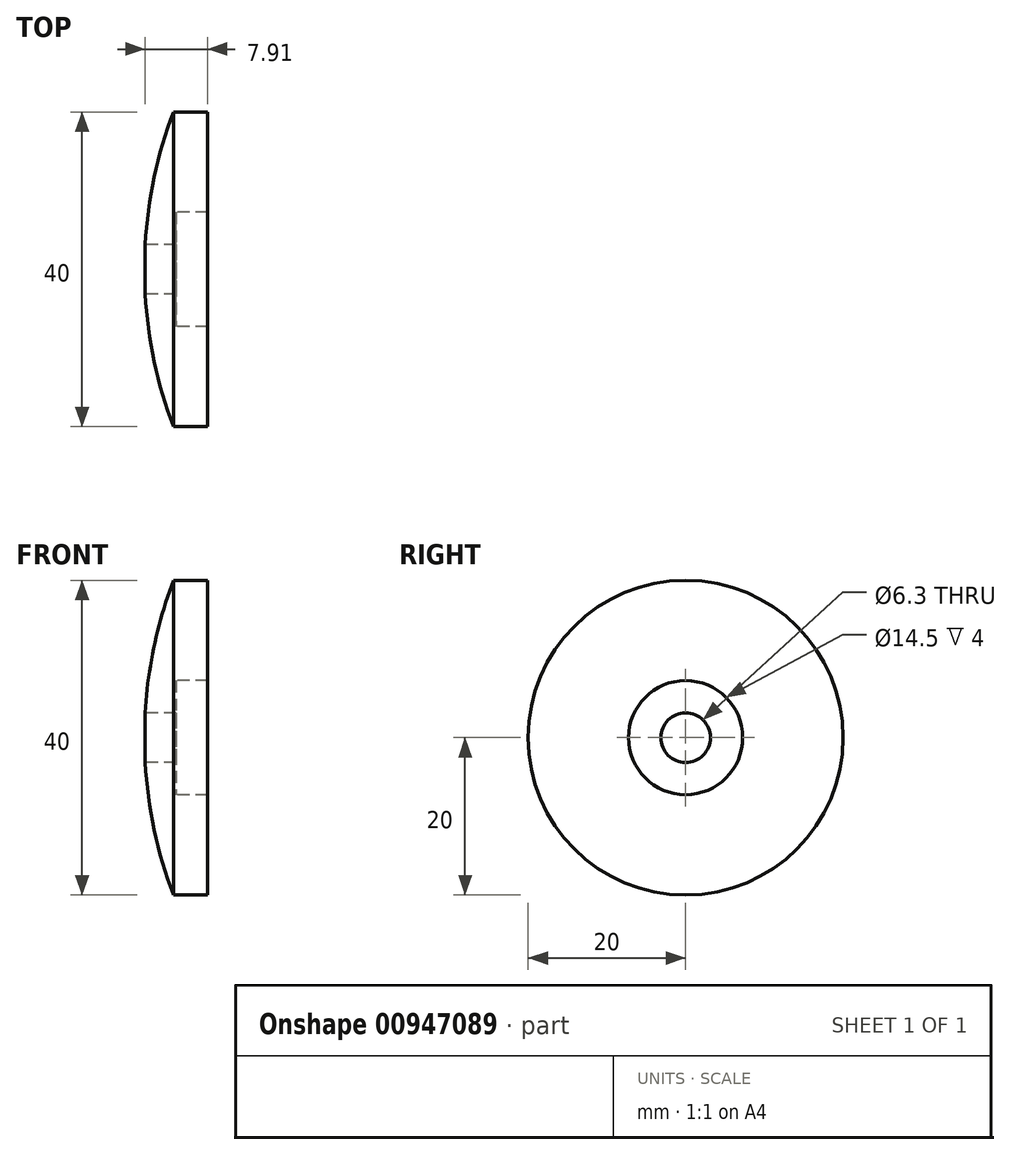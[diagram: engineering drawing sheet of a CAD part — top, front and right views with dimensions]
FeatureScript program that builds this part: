
annotation { "Feature Type Name" : "Feature", "Feature Type Description" : "" }
export const myFeature = defineFeature(function(context is Context, id is Id, definition is map)
    precondition{}
    {
        {
            var Q0;
            Q0=qCreatedBy(makeId("Front.planeOp"),FACE);
            var sketch = newSketch(context, id + "F0", { "sketchPlane" : qUnion([Q0])});
            skLineSegment(sketch, "E0", {"start": v(0, 0) * mm, "end": v(8, 0) * mm});
            skLineSegment(sketch, "E1", {"start": v(0, 3.15) * mm, "end": v(4, 3.15) * mm});
            skLineSegment(sketch, "E2", {"start": v(4, 3.15) * mm, "end": v(4, 7.25) * mm});
            skLineSegment(sketch, "E3", {"start": v(4, 7.25) * mm, "end": v(8, 7.25) * mm});
            skLineSegment(sketch, "E4", {"start": v(8, 7.25) * mm, "end": v(8, 20) * mm});
            skLineSegment(sketch, "E5", {"start": v(8, 20) * mm, "end": v(3.7, 20) * mm});
            skLineSegment(sketch, "E6.0.MirrorCS", {"start": v(0, -3.15) * mm, "end": v(4, -3.15) * mm});
            skLineSegment(sketch, "E7.0.MirrorCS", {"start": v(4, -3.15) * mm, "end": v(4, -7.25) * mm});
            skLineSegment(sketch, "E8.0.MirrorCS", {"start": v(4, -7.25) * mm, "end": v(8, -7.25) * mm});
            skLineSegment(sketch, "E9.0.MirrorCS", {"start": v(8, -7.25) * mm, "end": v(8, -20) * mm});
            skLineSegment(sketch, "E10.0.MirrorCS", {"start": v(8, -20) * mm, "end": v(3.7, -20) * mm});
            skArc(sketch, "E11", {"start": v(3.7, 20) * mm, "mid": v(0, 0) * mm, "end": v(3.7, -20) * mm});
            skSolve(sketch);
        }
        {
            var Q0;
            {var subQ4=sQuery(id+"F0.wireOp",EDGE,"E2");Q0=makeQuery(id+"F0.imprint","IMPRINT",FACE,{"disambiguationData":[TD([[makeQuery(id+"F0.imprint","IMPRINT",EDGE,{"derivedFrom":subQ4}),1.0]])]});}
            var Q1;
            Q1=sQuery(id+"F0.wireOp",EDGE,"E0");
            revolve(context, id + "F1", {"entities" : qUnion([Q0]), "axis" : qUnion([Q1]), "revolveType" : RevolveType.FULL});
        }
    });
